# Revit family: BE_77584_de_DE
name_source: partatom
category: Leuchten
revit_build: Autodesk Revit 2015 (Build: 20150704_0715(x64)
units: mm (PartAtom-declared; Revit-internal decimal feet)

## types (6) — shared parameters
AC/DC = AC/DC
Aktualisierung = 2016-03-07T04:09:05
BEGA_Dummy = Nein
BEGA_Intern = Ja
BEGA_Intern_Konstruktion = Ja
BEGA_Intern_an = Ja
BEGA_Intern_aus = Ja
Befestigungsabstand = 67 mm
Befestigungsbohrung = Ø 4,5 mm
Beschreibung = Scheinwerfer
Beschreibung_Sonderanfertigung = Hier können Sie Informationen zur Sonderanfertigung eintragen.
CE_Konformität = ja
Energieeffizienzklasse = LED A++ - A
Farbwiedergabeindex = Ra > 80
Frequenz = 0/50-60 Hz
Gewicht = 3.95 kg
Hersteller = BEGA
Lampe = LED 75.6 W
Lastklassifizierung = Beleuchtung
Lebensdauerkriterien = L70 = 50.000 h
Logo = BEGA_Logo.png
Material_02 = BEGA_Oberfläche_Silber_matt
Material_03 = BEGA_Oberfläche_Weiss_matt
Material_06 = BEGA_Oberfläche_Edelstahl_gebürstet
Material_09 = BEGA_Glas_klar
Material_15 = BEGA_Leuchtmedium_matt
Material_17 = BEGA_Reflektor
Material_18 = BEGA_Gummi_schwarz
Produktdatenblatt = http://www.bega.de
Scheinlast = 0 VA
Schutzart = IP 65
Schutzklasse = I
Sonderanfertigung = Nein
Spannung = 0 V
Typenbild = 77584.png
URL = http://www.bega.de
Umgebungstemperatur = 25 °C
zero-valued in all types: Vorgabe-Ansicht

## per-type parameters (varying)
| type | BEGA_IES1 | BEGA_IES2 | Bestellnummer | Farbtemperatur | LED_Modulbezeichnung | Lampenlichtstrom | Leuchtenlichtstrom | M_A | M_G | M_W | Modell |
| BEGA_77584_Weiß_K4 | Nein | Ja | 77584W | 4000 K | LED-0499/840 | 9500 lm | 7442 lm | Nein | Nein | Ja | 77584W |
| BEGA_77584_Grafit_K3 | Ja | Nein | 77584K3 | 3000 K | LED-0499/830 | 8850 lm | 6932 lm | Nein | Ja | Nein | 77584K3 |
| BEGA_77584_Silber_K3 | Ja | Nein | 77584AK3 | 3000 K | LED-0499/830 | 8850 lm | 6932 lm | Ja | Nein | Nein | 77584AK3 |
| BEGA_77584_Grafit_K4 | Nein | Ja | 77584 | 4000 K | LED-0499/840 | 9500 lm | 7442 lm | Nein | Ja | Nein | 77584 |
| BEGA_77584_Silber_K4 | Nein | Ja | 77584A | 4000 K | LED-0499/840 | 9500 lm | 7442 lm | Ja | Nein | Nein | 77584A |
| BEGA_77584_Weiß_K3 | Ja | Nein | 77584WK3 | 3000 K | LED-0499/830 | 8850 lm | 6932 lm | Nein | Nein | Ja | 77584WK3 |

## geometry (parser evidence)
native form markers: Blend x4, Sweep x8
no freeform markers — native parametric forms only
